# Revit family: Faucet-Kitchen-KOHLER-Tone-K-23765_1
name_source: partatom
category: Plumbing Fixtures
revit_build: Autodesk Revit 2017 (Build: 20160225_1515(x64)
units: mm (PartAtom-declared; Revit-internal decimal feet)

## family parameters
Cut with Voids When Loaded = No
Host = Face
OmniClass Number = 23.31.11.00
OmniClass Title = Faucets
Part Type = Normal
Room Calculation Point = No
Round Connector Dimension = Use Diameter
Shared = No

## types (6) — shared parameters
ADA Compliant = Yes
Assembly Code = D2010
CW Connection = Yes
Cold Water Inlet = Cold Water Inlet
Date Modified = 05/04/2021
Default Elevation = 36"
Description = Pull-down single-handle semi-professional kitchen sink faucet
Drain Included = No
Flow Rate = 2 GPM
HW Connection = Yes
Handle Clearance = 3 7/16"
Height = 22 1/8"
Hot Water Inlet = Hot Water Inlet
Length = 9 1/2"
Manufacturer = KOHLER Co.
Master Format 2014 = 22 41 39
Master Format 2014 Name = Residential Faucets, Supplies, and Trim
Material = Premium Metal Construction
Pressure = 60.00 psi
Product Documentation Link = https://www.us.kohler.com
Product Name = Tone
Product Page URL = http://www.us.kohler.com
Spout Reach = 9 1/2"
URL = https://www.us.kohler.com
Vent Connection = No
Waste Connection = No
Waste Water Outlet = Waste Water Outlet
WaterSense Certified = No
Width = 2 3/4"

## per-type parameters (varying)
| type | Finish | Model | Secondary Finish | Type |
| CP-Polished Chrome | Kohler-Metal-CP-Polished_Chrome | K-23765-CP | Kohler-Metal-CP-Polished_Chrome | 1 |
| VS-Vibrant Stainless | Kohler-Metal-VS-Vibrant_Stainless | K-23765-VS | Kohler-Metal-VS-Vibrant_Stainless | 2 |
| BL-Matte Black | Kohler-Metal-BL-Matte_Black | K-23765-BL | Kohler-Metal-BL-Matte_Black | 3 |
| 2MB-Vibrant Brushed Moderne Brass | Kohler-Metal-2MB-Vibrant_Brushed_Moderne_Brass | K-23765-2MB | Kohler-Metal-2MB-Vibrant_Brushed_Moderne_Brass | 4 |
| BMB-Matte Black With Moderne Brass | Kohler-Metal-2MB-Vibrant_Brushed_Moderne_Brass | K-23765-BMB | Kohler-Metal-BL-Matte_Black | 5 |
| CBL-Matte Black With Polished Chrome | Kohler-Metal-CP-Polished_Chrome | K-23765-CBL | Kohler-Metal-BL-Matte_Black | 6 |

## geometry (parser evidence)
native form markers: Sweep x6
no freeform markers — native parametric forms only
